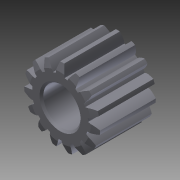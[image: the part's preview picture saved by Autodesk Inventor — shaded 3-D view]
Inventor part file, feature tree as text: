
AUTODESK INVENTOR PART (.ipt)
format: ipt  version: 2014 SP1 (Build 180222100, 222)  size: 430,592 bytes
history: native  units: mm (DEFAULTED — no unit token found)
features: sketch x4, extrude x3, plane x3, other x3, chamfer x3, projected_geometry x1
ambient origin geometry x8: Origin, YZ Plane, XZ Plane, XY Plane, X Axis, Y Axis, Z Axis, Center Point
bodies: Solid1 (feature_tree)
feature tree (17):
  extrude  "Extrusion1"  Depth=5.0mm TaperAngle=0.0deg
  plane  "Work Plane1"
  plane  "Work Plane2"
  plane  "Work Plane3"
  other  "Spur Gear"
  extrude  "Extrusion2"  Depth=76.2mm TaperAngle=0.0deg
  chamfer  "Chamfer3"  Distance=2.094395mm
  extrude  "Extrusion3"  Depth=9.0mm TaperAngle=0.0deg
  chamfer  "Chamfer2"  Distance=9.0mm
  chamfer  "Chamfer1"  Distance=5.0mm
  sketch  "Sketch1"  dims[d0=10.2mm d1=5.0mm d2=0.0mm]
  sketch  "Sketch2"  dims[d3=9.0mm d4=76.2mm d5=0.0mm d6=0.0mm d7=2.094395mm]
  other  "Srf1"
  sketch  "Sketch3"  dims[d9=0.0mm d14=0.0mm d15=9.0mm]
  sketch  "Sketch4"  dims[d16=0.0mm d17=0.0mm d18=0.0mm d19=9.0mm d20=5.0mm d22=25.4mm d23=0.0mm d26=0.254mm d27=3.175mm d28=45.0deg d29=1.0mm d30=3.175mm d31=15.0deg d32=1.0mm d33=3.175mm d34=15.0deg d35=3.0mm d36=0.0mm]
  projected_geometry  "Projected Loop1"
  other  "Pitch Diameter"
